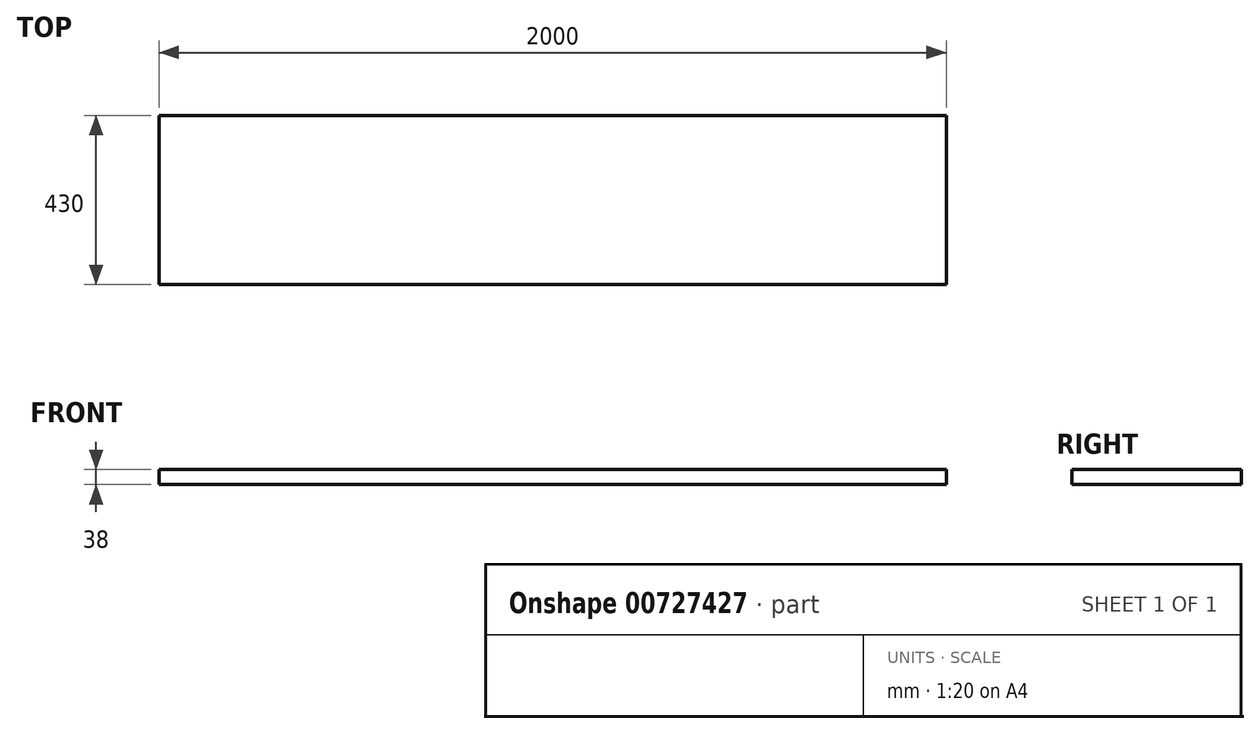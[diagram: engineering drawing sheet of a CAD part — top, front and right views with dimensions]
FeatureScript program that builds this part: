
annotation { "Feature Type Name" : "Feature", "Feature Type Description" : "" }
export const myFeature = defineFeature(function(context is Context, id is Id, definition is map)
    precondition{}
    {
        {
            var Q0;
            Q0=qCreatedBy(makeId("Top.planeOp"),FACE);
            var sketch = newSketch(context, id + "F0", { "sketchPlane" : qUnion([Q0])});
            skLineSegment(sketch, "E0.bottom", {"start": v(-998.1, -154.41) * mm, "end": v(1001.9, -154.41) * mm});
            skLineSegment(sketch, "E0.top", {"start": v(-998.1, -584.41) * mm, "end": v(1001.9, -584.41) * mm});
            skLineSegment(sketch, "E0.left", {"start": v(-998.1, -154.41) * mm, "end": v(-998.1, -584.41) * mm});
            skLineSegment(sketch, "E0.right", {"start": v(1001.9, -154.41) * mm, "end": v(1001.9, -584.41) * mm});
            skSolve(sketch);
        }
        {
            var Q0;
            Q0 = qSketchRegion(id + "F0", true);
            extrude(context, id + "F1", {"entities" : qUnion([Q0]), "depth" : 38 * mm, "offsetDistance" : 25 * mm});
        }
    });
